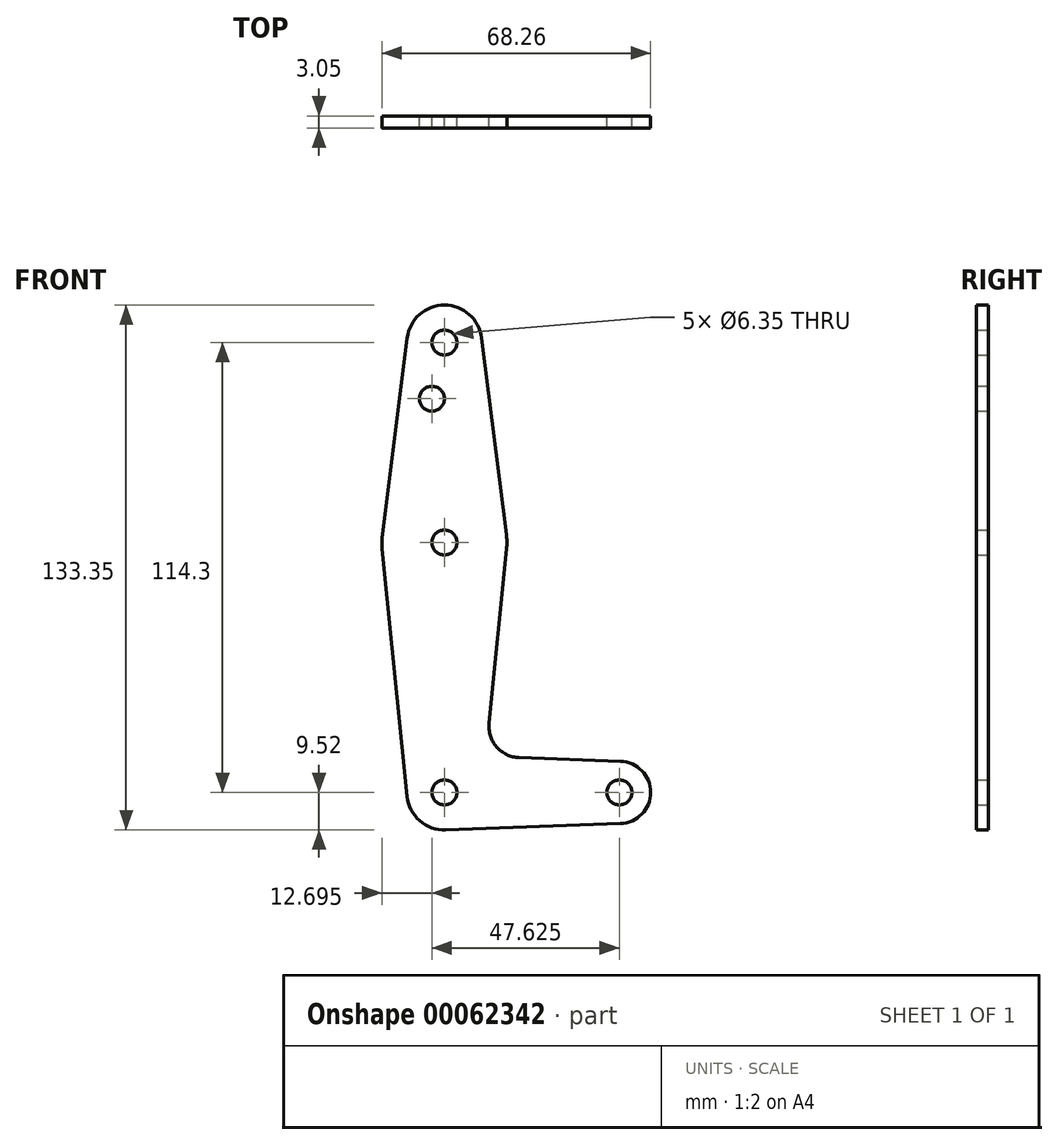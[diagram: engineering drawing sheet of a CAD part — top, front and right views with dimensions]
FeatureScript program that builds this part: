
annotation { "Feature Type Name" : "Feature", "Feature Type Description" : "" }
export const myFeature = defineFeature(function(context is Context, id is Id, definition is map)
    precondition{}
    {
        {
            var Q0;
            Q0=qCreatedBy(makeId("Front.planeOp"),FACE);
            var sketch = newSketch(context, id + "F0", { "sketchPlane" : qUnion([Q0])});
            skLineSegment(sketch, "E0", {"start": v(0, 0) * mm, "end": v(0, 114.3) * mm, "construction": true});
            skLineSegment(sketch, "E1", {"start": v(0, 0) * mm, "end": v(44.45, 0) * mm, "construction": true});
            skCircle(sketch, "E2", {"center": v(0, 114.3) * mm, "radius": 9.53 * mm});
            skCircle(sketch, "E3", {"center": v(0, 63.5) * mm, "radius": 15.88 * mm});
            skCircle(sketch, "E4", {"center": v(0, 0) * mm, "radius": 9.53 * mm});
            skCircle(sketch, "E5", {"center": v(44.45, 0) * mm, "radius": 7.94 * mm});
            skLineSegment(sketch, "E6", {"start": v(-15.8, 61.91) * mm, "end": v(-9.48, -0.95) * mm});
            skLineSegment(sketch, "E7", {"start": v(15.8, 61.91) * mm, "end": v(11.34, 17.6) * mm});
            skLineSegment(sketch, "E8", {"start": v(-9.45, 115.5) * mm, "end": v(-15.75, 65.48) * mm});
            skLineSegment(sketch, "E9", {"start": v(9.45, 115.5) * mm, "end": v(15.75, 65.48) * mm});
            skLineSegment(sketch, "E10", {"start": v(18.97, 8.85) * mm, "end": v(44.73, 7.93) * mm});
            skLineSegment(sketch, "E11", {"start": v(0.34, -9.52) * mm, "end": v(44.73, -7.93) * mm});
            skCircle(sketch, "E12", {"center": v(0, 114.3) * mm, "radius": 3.18 * mm});
            skCircle(sketch, "E13", {"center": v(-3.18, 100.03) * mm, "radius": 3.18 * mm});
            skCircle(sketch, "E14", {"center": v(0, 63.5) * mm, "radius": 3.18 * mm});
            skCircle(sketch, "E15", {"center": v(0, 0) * mm, "radius": 3.18 * mm});
            skCircle(sketch, "E16", {"center": v(44.45, 0) * mm, "radius": 3.18 * mm});
            skArc(sketch, "E17.filletArc", {"start": v(11.34, 17.6) * mm, "mid": v(13.26, 11.57) * mm, "end": v(18.97, 8.85) * mm});
            skSolve(sketch);
        }
        {
            var Q0;
            Q0 = qSketchRegion(id + "F0", true);
            extrude(context, id + "F1", {"entities" : qUnion([Q0]), "depth" : 3.05 * mm});
        }
    });
